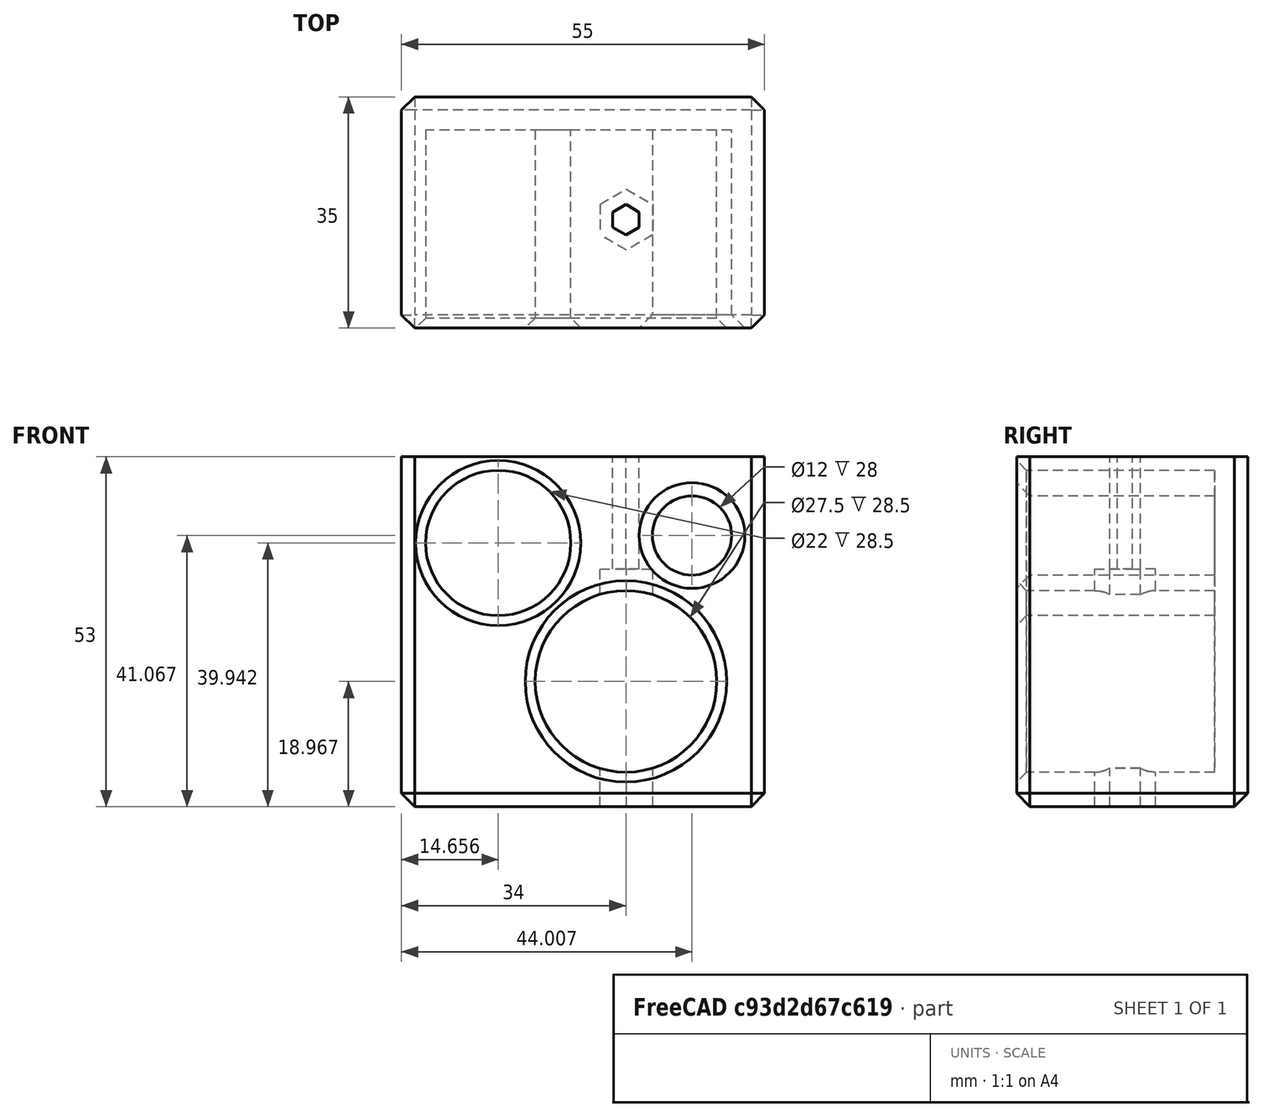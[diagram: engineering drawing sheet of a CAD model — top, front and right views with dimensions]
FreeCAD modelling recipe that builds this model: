
FCSTD DOCUMENT  (FreeCAD 0.19R)
Label: SharpieHolder
License: All rights reserved
LicenseURL: http://en.wikipedia.org/wiki/All_rights_reserved
objects: Sketcher::SketchObject×4, PartDesign::Pocket×3, PartDesign::Chamfer×3, PartDesign::Pad×1, PartDesign::Body×1, Mesh::Feature×1
note: 19 computed .brp shape members not serialized (recipe doc carries the construction recipe); baked Part::Feature solids carry a one-line shape summary decoded from their .brp

FEATURE [Sketcher::SketchObject] Sketch
  FullyConstrained = true
  MapMode = 5
  Placement = pos=(0,0,0) rot=(1,0,0;1.5708rad)
  Support = -> [XZ_Plane]
  sketch-geometry (4):
    g0: LineSegment StartX=-27.5 StartY=0 StartZ=0 EndX=27.5 EndY=0 EndZ=0
    g1: LineSegment StartX=27.5 StartY=0 StartZ=0 EndX=27.5 EndY=-53 EndZ=0
    g2: LineSegment StartX=27.5 StartY=-53 StartZ=0 EndX=-27.5 EndY=-53 EndZ=0
    g3: LineSegment StartX=-27.5 StartY=-53 StartZ=0 EndX=-27.5 EndY=0 EndZ=0
  constraints (11):
    c: Coincident(g0,g1)
    c: Coincident(g1,g2)
    c: Coincident(g2,g3)
    c: Coincident(g3,g0)
    c: Horizontal(g2)
    c: Vertical(g1)
    c: Vertical(g3)
    c: PointOnObject(g0,g-1)
    c: Symmetric(g0,g0,g-2)
    c: Distance(g1) = 53
    c: Distance(g0) = 55
FEATURE [PartDesign::Pad] Pad
  Direction = (1,1,1)
  Length = 35
  Length2 = 100
  Placement = pos=(0,0,0) rot=(1,0,0;1.5708rad)
  Profile = -> Sketch
  Type = 0
FEATURE [Sketcher::SketchObject] Sketch001
  FullyConstrained = false
  MapMode = 5
  Placement = pos=(0,-35,1.55e-14) rot=(1,0,0;1.5708rad)
  Support = -> [Pad]
  sketch-geometry (3):
    g0: Circle CenterX=-12.8436 CenterY=-13.0583 CenterZ=0 NormalX=0 NormalY=0 NormalZ=1 AngleXU=0 Radius=11
    g1: Circle CenterX=16.5065 CenterY=-11.9329 CenterZ=0 NormalX=0 NormalY=0 NormalZ=1 AngleXU=0 Radius=6
    g2: Circle CenterX=6.5 CenterY=-34.0328 CenterZ=0 NormalX=0 NormalY=0 NormalZ=1 AngleXU=0 Radius=13.75
  constraints (4):
    c: Diameter(g0) = 22
    c: Diameter(g1) = 12
    c: Diameter(g2) = 27.5
    c: DistanceX(g2) = 6.5
FEATURE [PartDesign::Pocket] Pocket
  BaseFeature = -> Pad
  Length = 30
  Length2 = 100
  Placement = pos=(0,0,0) rot=(1,0,0;1.5708rad)
  Profile = -> Sketch001
  Type = 0
FEATURE [PartDesign::Chamfer] Chamfer
  Angle = 45
  Base = -> Pocket [Edge8,Edge5,Edge11,Edge9,Edge6,Edge7,Edge12,Edge10]
  BaseFeature = -> Pocket
  ChamferType = 0
  FlipDirection = false
  Placement = pos=(0,0,0) rot=(1,0,0;1.5708rad)
  Size = 2
  Size2 = 1
  SupportTransform = false
FEATURE [PartDesign::Chamfer] Chamfer001
  Angle = 45
  Base = -> Chamfer [Edge21,Edge20]
  BaseFeature = -> Chamfer
  ChamferType = 0
  FlipDirection = false
  Placement = pos=(0,0,0) rot=(1,0,0;1.5708rad)
  Size = 1.5
  Size2 = 1
  SupportTransform = false
FEATURE [Sketcher::SketchObject] Sketch002
  FullyConstrained = false
  MapMode = 5
  Placement = pos=(0,-4.1e-14,-53) rot=(1,0,0;3.14159rad)
  Support = -> [Chamfer001]
  sketch-geometry (7):
    g0: LineSegment StartX=6.5 StartY=16.2798 StartZ=0 EndX=8.5 EndY=17.4345 EndZ=0
    g1: LineSegment StartX=8.5 StartY=17.4345 StartZ=0 EndX=8.5 EndY=19.744 EndZ=0
    g2: LineSegment StartX=8.5 StartY=19.744 StartZ=0 EndX=6.5 EndY=20.8987 EndZ=0
    g3: LineSegment StartX=6.5 StartY=20.8987 StartZ=0 EndX=4.5 EndY=19.744 EndZ=0
    g4: LineSegment StartX=4.5 StartY=19.744 StartZ=0 EndX=4.5 EndY=17.4345 EndZ=0
    g5: LineSegment StartX=4.5 StartY=17.4345 StartZ=0 EndX=6.5 EndY=16.2798 EndZ=0
    g6: Circle CenterX=6.5 CenterY=18.5892 CenterZ=0 NormalX=0 NormalY=0 NormalZ=1 AngleXU=0 Radius=2.3094
  constraints (16):
    c: Coincident(g0,g1)
    c: Coincident(g1,g2)
    c: Coincident(g2,g3)
    c: Coincident(g3,g4)
    c: Coincident(g4,g5)
    c: Coincident(g5,g0)
    c: Equal(g0, g1-g5) x5
    c: PointOnObject(g0,g6)
    c: PointOnObject(g1,g6)
    c: PointOnObject(g2,g6)
    c: PointOnObject(g3,g6)
    c: PointOnObject(g4,g6)
    c: PointOnObject(g5,g6)
    c: Distance(g1,g3) = 4
    c: Vertical(g1)
    c: DistanceX(g6) = 6.5
FEATURE [PartDesign::Pocket] Pocket001
  BaseFeature = -> Chamfer001
  Length = 5
  Length2 = 100
  Placement = pos=(0,0,0) rot=(1,0,0;1.5708rad)
  Profile = -> Sketch002
  Type = 1
FEATURE [Sketcher::SketchObject] Sketch003
  FullyConstrained = false
  MapMode = 5
  Placement = pos=(0,-4.69e-14,-53) rot=(1,0,0;3.14159rad)
  Support = -> [Pocket001]
  sketch-geometry (7):
    g0: LineSegment StartX=10.5481 StartY=16.2658 StartZ=0 EndX=10.5481 EndY=20.8846 EndZ=0
    g1: LineSegment StartX=10.5481 StartY=20.8846 StartZ=0 EndX=6.54805 EndY=23.194 EndZ=0
    g2: LineSegment StartX=6.54805 StartY=23.194 StartZ=0 EndX=2.54805 EndY=20.8846 EndZ=0
    g3: LineSegment StartX=2.54805 StartY=20.8846 StartZ=0 EndX=2.54805 EndY=16.2658 EndZ=0
    g4: LineSegment StartX=2.54805 StartY=16.2658 StartZ=0 EndX=6.54805 EndY=13.9564 EndZ=0
    g5: LineSegment StartX=6.54805 StartY=13.9564 StartZ=0 EndX=10.5481 EndY=16.2658 EndZ=0
    g6: Circle CenterX=6.54805 CenterY=18.5752 CenterZ=0 NormalX=0 NormalY=0 NormalZ=1 AngleXU=0 Radius=4.6188
  constraints (15):
    c: Coincident(g0,g1)
    c: Coincident(g1,g2)
    c: Coincident(g2,g3)
    c: Coincident(g3,g4)
    c: Coincident(g4,g5)
    c: Coincident(g5,g0)
    c: Equal(g0, g1-g5) x5
    c: PointOnObject(g0,g6)
    c: PointOnObject(g1,g6)
    c: PointOnObject(g2,g6)
    c: PointOnObject(g3,g6)
    c: PointOnObject(g4,g6)
    c: PointOnObject(g5,g6)
    c: Vertical(g0)
    c: Distance(g0,g3) = 8
FEATURE [PartDesign::Pocket] Pocket002
  BaseFeature = -> Pocket001
  Length = 36
  Length2 = 100
  Placement = pos=(0,0,0) rot=(1,0,0;1.5708rad)
  Profile = -> Sketch003
  Type = 0
FEATURE [PartDesign::Chamfer] Chamfer002
  Angle = 45
  Base = -> Pocket002 [Edge6]
  BaseFeature = -> Pocket002
  ChamferType = 0
  FlipDirection = false
  Placement = pos=(0,0,0) rot=(1,0,0;1.5708rad)
  Size = 2
  Size2 = 1
  SupportTransform = false
FEATURE [PartDesign::Body] Body
  Group = -> [Sketch,Pad,Sketch001,Pocket,Chamfer,Chamfer001,Sketch002,Pocket001,Sketch003,Pocket002,Chamfer002]
  Origin = -> Origin
  Tip = -> Chamfer002
FEATURE [Mesh::Feature] Mesh  label="Chamfer002 (Meshed)"
